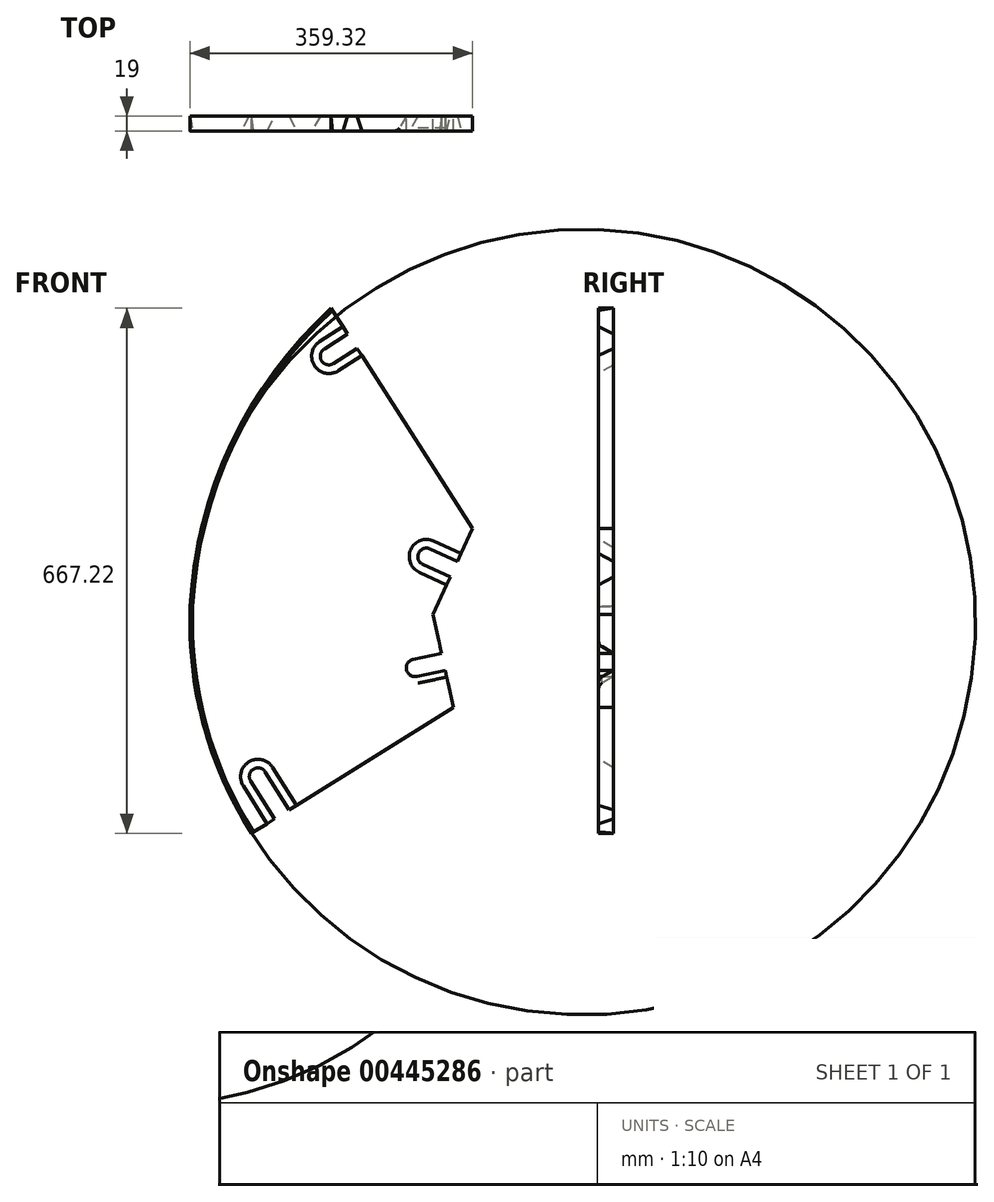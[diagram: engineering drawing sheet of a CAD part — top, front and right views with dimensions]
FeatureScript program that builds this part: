
annotation { "Feature Type Name" : "Feature", "Feature Type Description" : "" }
export const myFeature = defineFeature(function(context is Context, id is Id, definition is map)
    precondition{}
    {
        {
            var Q0;
            Q0=qCreatedBy(makeId("Front.planeOp"),FACE);
            var sketch = newSketch(context, id + "F0", { "sketchPlane" : qUnion([Q0])});
            skArc(sketch, "E0", {"start": v(-0.07, 333.61) * mm, "mid": v(-127.03, 161.95) * mm, "end": v(-179.26, -45.08) * mm});
            skArc(sketch, "E1", {"start": v(-179.26, -45.08) * mm, "mid": v(-162.39, -195.32) * mm, "end": v(-101.3, -333.61) * mm});
            skLineSegment(sketch, "E2", {"start": v(160.4, 12.03) * mm, "end": v(125.56, 27.86) * mm});
            skLineSegment(sketch, "E3", {"start": v(116.46, 7.83) * mm, "end": v(151.18, -7.94) * mm});
            skArc(sketch, "E4", {"start": v(125.56, 27.86) * mm, "mid": v(111, 22.39) * mm, "end": v(116.46, 7.83) * mm});
            skLineSegment(sketch, "E5", {"start": v(140.15, -104.86) * mm, "end": v(104, -112.63) * mm});
            skLineSegment(sketch, "E6", {"start": v(144.82, -126.36) * mm, "end": v(108.63, -134.14) * mm});
            skArc(sketch, "E7", {"start": v(104, -112.63) * mm, "mid": v(95.57, -125.7) * mm, "end": v(108.63, -134.14) * mm});
            skArc(sketch, "E8", {"start": v(-8.84, 281.87) * mm, "mid": v(-12.18, 266.67) * mm, "end": v(3.02, 263.34) * mm});
            skLineSegment(sketch, "E9", {"start": v(20.92, 300.92) * mm, "end": v(-8.84, 281.87) * mm});
            skLineSegment(sketch, "E10", {"start": v(3.02, 263.34) * mm, "end": v(32.81, 282.41) * mm});
            skArc(sketch, "E11", {"start": v(-83.86, -255.5) * mm, "mid": v(-99.03, -252.04) * mm, "end": v(-102.48, -267.21) * mm});
            skLineSegment(sketch, "E12", {"start": v(-83.86, -255.5) * mm, "end": v(-53.48, -303.76) * mm});
            skLineSegment(sketch, "E13", {"start": v(-102.48, -267.21) * mm, "end": v(-72.15, -315.41) * mm});
            skLineSegment(sketch, "E14", {"start": v(-101.3, -333.61) * mm, "end": v(-72.15, -315.41) * mm});
            skLineSegment(sketch, "E15", {"start": v(-53.48, -303.76) * mm, "end": v(155.06, -173.57) * mm});
            skLineSegment(sketch, "E16", {"start": v(155.06, -173.57) * mm, "end": v(144.82, -126.36) * mm});
            skLineSegment(sketch, "E17", {"start": v(140.15, -104.86) * mm, "end": v(129.38, -55.21) * mm});
            skLineSegment(sketch, "E18", {"start": v(129.38, -55.21) * mm, "end": v(151.18, -7.94) * mm});
            skLineSegment(sketch, "E19", {"start": v(160.4, 12.03) * mm, "end": v(179.66, 53.78) * mm});
            skLineSegment(sketch, "E20", {"start": v(179.66, 53.78) * mm, "end": v(32.81, 282.41) * mm});
            skLineSegment(sketch, "E21", {"start": v(20.92, 300.92) * mm, "end": v(-0.07, 333.61) * mm});
            skSolve(sketch);
        }
        {
            var Q0;
            Q0 = qSketchRegion(id + "F0", true);
            extrude(context, id + "F1", {"entities" : qUnion([Q0]), "depth" : 19 * mm});
        }
        {
            var Q0;
            Q0=makeQuery(id+"F1.opExtrude","SWEPT_FACE",FACE,{"disambiguationData":[OSD([sQuery(id+"F0.wireOp",EDGE,"E14")])]});
            var sketch = newSketch(context, id + "F2", { "sketchPlane" : qUnion([Q0])});
            skLineSegment(sketch, "E22", {"start": v(-228.23, 0) * mm, "end": v(-228.23, 19) * mm});
            skLineSegment(sketch, "E23", {"start": v(-228.23, 19) * mm, "end": v(-239.2, 19) * mm});
            skLineSegment(sketch, "E24", {"start": v(-239.2, 19) * mm, "end": v(-228.23, 0) * mm});
            skSolve(sketch);
        }
        {
            var Q0;
            Q0 = qSketchRegion(id + "F2", true);
            var Q1;
            Q1=makeQuery(id+"F1.opExtrude","CAP_EDGE",EDGE,{"disambiguationData":[OSD([sQuery(id+"F0.wireOp",EDGE,"E13")])],"isStart":false});
            var Q2;
            Q2=makeQuery(id+"F1.opExtrude","CAP_EDGE",EDGE,{"disambiguationData":[OSD([sQuery(id+"F0.wireOp",EDGE,"E11")])],"isStart":false});
            var Q3;
            Q3=makeQuery(id+"F1.opExtrude","CAP_EDGE",EDGE,{"disambiguationData":[OSD([sQuery(id+"F0.wireOp",EDGE,"E12")])],"isStart":false});
            sweep(context, id + "F3", {"operationType" : NewBodyOperationType.REMOVE, "profiles" : qUnion([Q0]), "path" : qUnion([Q1, Q2, Q3])});
        }
        {
            var Q0;
            Q0=makeQuery(id+"F1.opExtrude","SWEPT_FACE",FACE,{"disambiguationData":[OSD([sQuery(id+"F0.wireOp",EDGE,"E16")])]});
            var sketch = newSketch(context, id + "F4", { "sketchPlane" : qUnion([Q0])});
            skLineSegment(sketch, "E25", {"start": v(0, -154.2) * mm, "end": v(-19, -154.2) * mm});
            skLineSegment(sketch, "E26", {"start": v(-19, -154.2) * mm, "end": v(-19, -165.17) * mm});
            skLineSegment(sketch, "E27", {"start": v(-19, -165.17) * mm, "end": v(0, -154.2) * mm});
            skSolve(sketch);
        }
        {
            var Q0;
            Q0 = qSketchRegion(id + "F4", true);
            var Q1;
            Q1=makeQuery(id+"F1.opExtrude","CAP_EDGE",EDGE,{"disambiguationData":[OSD([sQuery(id+"F0.wireOp",EDGE,"E6")])],"isStart":false});
            var Q2;
            Q2=makeQuery(id+"F1.opExtrude","CAP_EDGE",EDGE,{"disambiguationData":[OSD([sQuery(id+"F0.wireOp",EDGE,"E7")])],"isStart":false});
            var Q3;
            Q3=makeQuery(id+"F1.opExtrude","CAP_EDGE",EDGE,{"disambiguationData":[OSD([sQuery(id+"F0.wireOp",EDGE,"E5")])],"isStart":false});
            sweep(context, id + "F5", {"operationType" : NewBodyOperationType.REMOVE, "profiles" : qUnion([Q0]), "path" : qUnion([Q1, Q2, Q3])});
        }
        {
            var Q0;
            Q0=makeQuery(id+"F1.opExtrude","SWEPT_FACE",FACE,{"disambiguationData":[OSD([sQuery(id+"F0.wireOp",EDGE,"E18")])]});
            var sketch = newSketch(context, id + "F6", { "sketchPlane" : qUnion([Q0])});
            skLineSegment(sketch, "E28", {"start": v(0, 56.13) * mm, "end": v(-19, 56.13) * mm});
            skLineSegment(sketch, "E29", {"start": v(-19, 56.13) * mm, "end": v(-19, 45.16) * mm});
            skLineSegment(sketch, "E30", {"start": v(-19, 45.16) * mm, "end": v(0, 56.13) * mm});
            skSolve(sketch);
        }
        {
            var Q0;
            Q0 = qSketchRegion(id + "F6", true);
            var Q1;
            Q1=makeQuery(id+"F1.opExtrude","CAP_EDGE",EDGE,{"disambiguationData":[OSD([sQuery(id+"F0.wireOp",EDGE,"E3")])],"isStart":false});
            var Q2;
            Q2=makeQuery(id+"F1.opExtrude","CAP_EDGE",EDGE,{"disambiguationData":[OSD([sQuery(id+"F0.wireOp",EDGE,"E4")])],"isStart":false});
            var Q3;
            Q3=makeQuery(id+"F1.opExtrude","CAP_EDGE",EDGE,{"disambiguationData":[OSD([sQuery(id+"F0.wireOp",EDGE,"E2")])],"isStart":false});
            sweep(context, id + "F7", {"operationType" : NewBodyOperationType.REMOVE, "profiles" : qUnion([Q0]), "path" : qUnion([Q1, Q2, Q3])});
        }
        {
            var Q0;
            Q0=makeQuery(id+"F1.opExtrude","SWEPT_FACE",FACE,{"disambiguationData":[OSD([sQuery(id+"F0.wireOp",EDGE,"E20")])]});
            var sketch = newSketch(context, id + "F8", { "sketchPlane" : qUnion([Q0])});
            skLineSegment(sketch, "E31", {"start": v(0, 219.9) * mm, "end": v(-19, 219.9) * mm});
            skLineSegment(sketch, "E32", {"start": v(-19, 219.9) * mm, "end": v(-19, 208.92) * mm});
            skLineSegment(sketch, "E33", {"start": v(-19, 208.92) * mm, "end": v(0, 219.9) * mm});
            skSolve(sketch);
        }
        {
            var Q0;
            Q0 = qSketchRegion(id + "F8", true);
            var Q1;
            Q1=makeQuery(id+"F1.opExtrude","CAP_EDGE",EDGE,{"disambiguationData":[OSD([sQuery(id+"F0.wireOp",EDGE,"E10")])],"isStart":false});
            var Q2;
            Q2=makeQuery(id+"F1.opExtrude","CAP_EDGE",EDGE,{"disambiguationData":[OSD([sQuery(id+"F0.wireOp",EDGE,"E8")])],"isStart":false});
            var Q3;
            Q3=makeQuery(id+"F1.opExtrude","CAP_EDGE",EDGE,{"disambiguationData":[OSD([sQuery(id+"F0.wireOp",EDGE,"E9")])],"isStart":false});
            sweep(context, id + "F9", {"operationType" : NewBodyOperationType.REMOVE, "profiles" : qUnion([Q0]), "path" : qUnion([Q1, Q2, Q3])});
        }
        {
            var Q0;
            Q0=makeQuery(id+"F1.opExtrude","SWEPT_FACE",FACE,{"disambiguationData":[OSD([sQuery(id+"F0.wireOp",EDGE,"E21")])]});
            var sketch = newSketch(context, id + "F10", { "sketchPlane" : qUnion([Q0])});
            skLineSegment(sketch, "E34", {"start": v(0, 280.74) * mm, "end": v(-19, 280.74) * mm});
            skLineSegment(sketch, "E35", {"start": v(-19, 280.74) * mm, "end": v(-19, 277.39) * mm});
            skLineSegment(sketch, "E36", {"start": v(-19, 277.39) * mm, "end": v(0, 280.74) * mm});
            skSolve(sketch);
        }
        {
            var Q0;
            Q0 = qSketchRegion(id + "F10", true);
            var Q1;
            Q1=makeQuery(id+"F1.opExtrude","CAP_EDGE",EDGE,{"disambiguationData":[OSD([sQuery(id+"F0.wireOp",EDGE,"E0")])],"isStart":false});
            var Q2;
            Q2=makeQuery(id+"F1.opExtrude","CAP_EDGE",EDGE,{"disambiguationData":[OSD([sQuery(id+"F0.wireOp",EDGE,"E1")])],"isStart":false});
            sweep(context, id + "F11", {"operationType" : NewBodyOperationType.REMOVE, "profiles" : qUnion([Q0]), "path" : qUnion([Q1, Q2])});
        }
        {
            var Q0;
            Q0=makeQuery(id+"F3.boolean.opBoolean","COPY",EDGE,{"derivedFrom":makeQuery(id+"F3.opSweep","SWEPT_EDGE",EDGE,{"disambiguationData":[OSD([sQuery(id+"F0.wireOp",EDGE,"E13"),sQuery(id+"F0.wireOp",EDGE,"E14"),sQuery(id+"F2.wireOp",EDGE,"E23"),sQuery(id+"F2.wireOp",EDGE,"E24")])]})});
            var Q1;
            Q1=makeQuery(id+"F5.boolean.opBoolean","COPY",EDGE,{"derivedFrom":makeQuery(id+"F5.opSweep","SWEPT_EDGE",EDGE,{"disambiguationData":[OSD([sQuery(id+"F0.wireOp",EDGE,"E5"),sQuery(id+"F0.wireOp",EDGE,"E16"),sQuery(id+"F4.wireOp",EDGE,"E26"),sQuery(id+"F4.wireOp",EDGE,"E27")])]})});
            var Q2;
            Q2=makeQuery(id+"F7.boolean.opBoolean","COPY",EDGE,{"derivedFrom":makeQuery(id+"F7.opSweep","SWEPT_EDGE",EDGE,{"disambiguationData":[OSD([sQuery(id+"F0.wireOp",EDGE,"E3"),sQuery(id+"F0.wireOp",EDGE,"E18"),sQuery(id+"F6.wireOp",EDGE,"E29"),sQuery(id+"F6.wireOp",EDGE,"E30")])]})});
            var Q3;
            Q3=makeQuery(id+"F9.boolean.opBoolean","COPY",EDGE,{"derivedFrom":makeQuery(id+"F9.opSweep","SWEPT_EDGE",EDGE,{"disambiguationData":[OSD([sQuery(id+"F0.wireOp",EDGE,"E9"),sQuery(id+"F0.wireOp",EDGE,"E20"),sQuery(id+"F8.wireOp",EDGE,"E32"),sQuery(id+"F8.wireOp",EDGE,"E33")])]})});
            fillet(context, id + "F12", {"entities" : qUnion([Q0, Q1, Q2, Q3]), "radius" : 8 * mm, "tangentPropagation" : true, "allowEdgeOverflow" : false});
        }
    });
